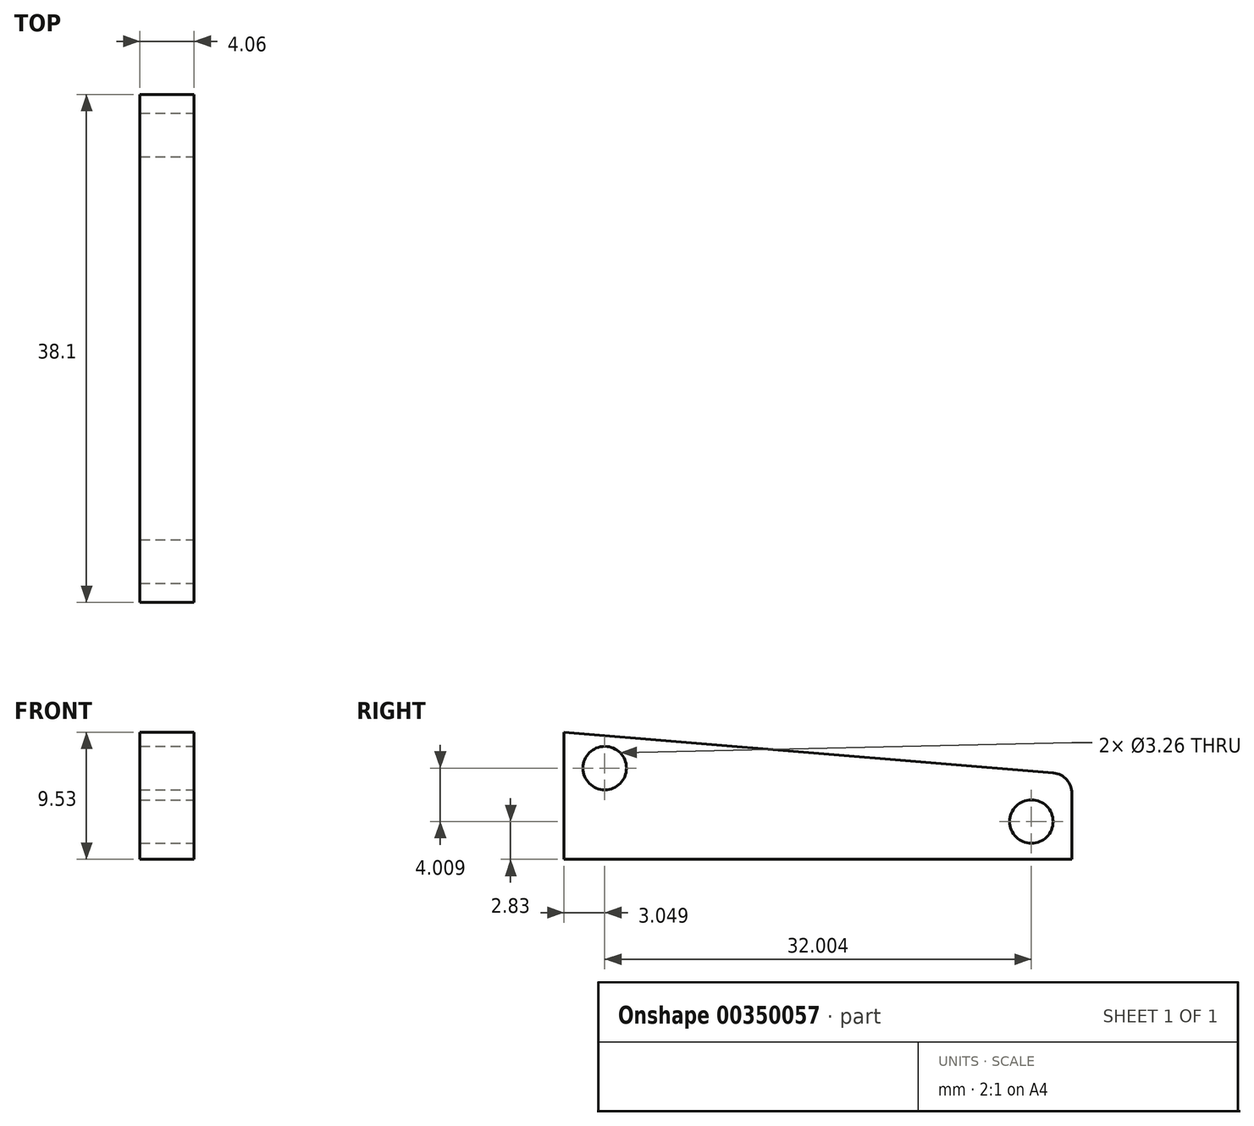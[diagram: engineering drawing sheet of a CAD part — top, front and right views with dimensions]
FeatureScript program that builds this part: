
annotation { "Feature Type Name" : "Feature", "Feature Type Description" : "" }
export const myFeature = defineFeature(function(context is Context, id is Id, definition is map)
    precondition{}
    {
        {
            var Q0;
            Q0=qCreatedBy(makeId("Right.planeOp"),FACE);
            var sketch = newSketch(context, id + "F0", { "sketchPlane" : qUnion([Q0])});
            skLineSegment(sketch, "E0", {"start": v(-20.6, 0) * mm, "end": v(-20.6, 9.53) * mm});
            skLineSegment(sketch, "E1", {"start": v(-20.6, 9.53) * mm, "end": v(17.5, 6.35) * mm});
            skLineSegment(sketch, "E2", {"start": v(17.5, 6.35) * mm, "end": v(17.5, 0) * mm});
            skLineSegment(sketch, "E3", {"start": v(17.5, 0) * mm, "end": v(-20.6, 0) * mm});
            skSolve(sketch);
        }
        {
            var Q0;
            Q0 = qSketchRegion(id + "F0", true);
            extrude(context, id + "F1", {"entities" : qUnion([Q0]), "depth" : 4.06 * mm});
        }
        {
            var Q0;
            Q0=makeQuery(id+"F1.opExtrude","CAP_FACE",FACE,{"disambiguationData":[OSD([sQuery(id+"F0.wireOp",EDGE,"E0"),sQuery(id+"F0.wireOp",EDGE,"E1"),sQuery(id+"F0.wireOp",EDGE,"E2"),sQuery(id+"F0.wireOp",EDGE,"E3")])],"isStart":false});
            var sketch = newSketch(context, id + "F2", { "sketchPlane" : qUnion([Q0])});
            skPoint(sketch, "E4", {"position": v(-17.56, 6.84) * mm});
            skPoint(sketch, "E5", {"position": v(14.44, 2.83) * mm});
            skSolve(sketch);
        }
        {
            var Q0;
            Q0=sQuery(id+"F2.wireOp",VERTEX,"E4");
            var Q1;
            Q1=sQuery(id+"F2.wireOp",VERTEX,"E5");
            var Q2;
            Q2=makeQuery(id+"F1.opExtrude","SWEPT_BODY",BODY,{"disambiguationData":[OSD([sQuery(id+"F0.wireOp",EDGE,"E0"),sQuery(id+"F0.wireOp",EDGE,"E1"),sQuery(id+"F0.wireOp",EDGE,"E2"),sQuery(id+"F0.wireOp",EDGE,"E3")])]});
            hole(context, id + "F3", {"style" : HoleStyle.SIMPLE, "endStyle" : HoleEndStyle.THROUGH, "standardTappedOrClearance" : lookupTablePath({ "standard" : "ANSI", "fit" : "Normal (ASME)", "size" : "#4", "type" : "Clearance" }), "standardBlindInLast" : lookupTablePath({ "fit" : "Free", "standard" : "ANSI", "size" : "#4", "type" : "Clearance" }), "holeDiameter" : 3.26 * mm, "isTappedThrough" : true, "tappedDepth" : 12.7 * mm, "tapClearance" : 3, "locations" : qUnion([Q0, Q1]), "scope" : qUnion([Q2])});
        }
        {
            var Q0;
            Q0=makeQuery(id+"F1.opExtrude","SWEPT_EDGE",EDGE,{"disambiguationData":[OSD([sQuery(id+"F0.wireOp",EDGE,"E1"),sQuery(id+"F0.wireOp",EDGE,"E2")])]});
            fillet(context, id + "F4", {"entities" : qUnion([Q0]), "radius" : 1.52 * mm, "tangentPropagation" : true, "allowEdgeOverflow" : false});
        }
    });
